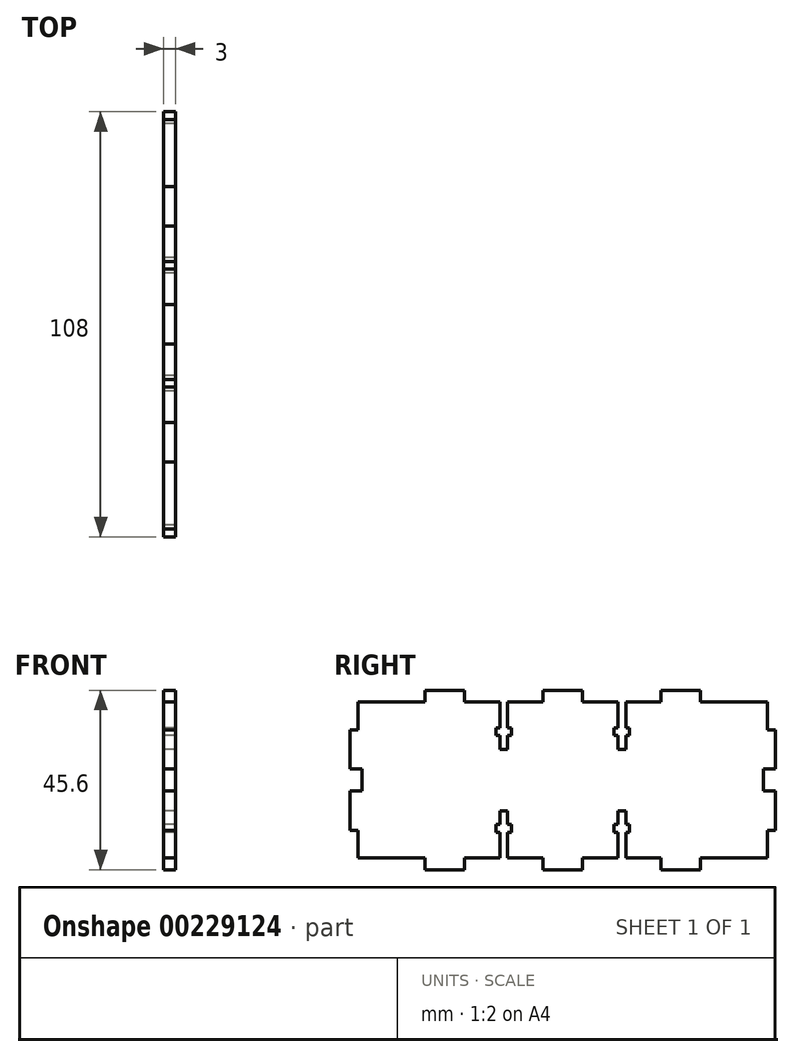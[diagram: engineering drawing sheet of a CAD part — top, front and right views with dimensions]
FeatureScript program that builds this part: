
annotation { "Feature Type Name" : "Feature", "Feature Type Description" : "" }
export const myFeature = defineFeature(function(context is Context, id is Id, definition is map)
    precondition{}
    {
        {
            var Q0;
            Q0=qCreatedBy(makeId("Right.planeOp"),FACE);
            var sketch = newSketch(context, id + "F0", { "sketchPlane" : qUnion([Q0])});
            skLineSegment(sketch, "E0", {"start": v(2.73, 33.75) * mm, "end": v(2.73, -11.85) * mm, "construction": true});
            skLineSegment(sketch, "E1.MirrorCS", {"start": v(16.73, 22.25) * mm, "end": v(15.73, 22.25) * mm});
            skLineSegment(sketch, "E2.MirrorCS", {"start": v(19.73, 22.25) * mm, "end": v(18.73, 22.25) * mm});
            skLineSegment(sketch, "E3.MirrorCS", {"start": v(18.73, 24.25) * mm, "end": v(19.73, 24.25) * mm});
            skLineSegment(sketch, "E4.MirrorCS", {"start": v(19.73, 24.25) * mm, "end": v(19.73, 22.25) * mm});
            skLineSegment(sketch, "E5.MirrorCS", {"start": v(19.73, -2.35) * mm, "end": v(19.73, -0.35) * mm});
            skLineSegment(sketch, "E6.MirrorCS", {"start": v(18.73, -2.35) * mm, "end": v(19.73, -2.35) * mm});
            skLineSegment(sketch, "E7.MirrorCS", {"start": v(15.73, 22.25) * mm, "end": v(15.73, 24.25) * mm});
            skLineSegment(sketch, "E8.MirrorCS", {"start": v(15.73, 24.25) * mm, "end": v(16.73, 24.25) * mm});
            skLineSegment(sketch, "E9.MirrorCS", {"start": v(19.73, -0.35) * mm, "end": v(18.73, -0.35) * mm});
            skLineSegment(sketch, "E10.MirrorCS", {"start": v(15.73, -0.35) * mm, "end": v(15.73, -2.35) * mm});
            skLineSegment(sketch, "E11.MirrorCS", {"start": v(16.73, -0.35) * mm, "end": v(15.73, -0.35) * mm});
            skLineSegment(sketch, "E12.MirrorCS", {"start": v(18.73, 22.25) * mm, "end": v(18.73, 18.75) * mm});
            skLineSegment(sketch, "E13.MirrorCS", {"start": v(53.73, 8.15) * mm, "end": v(53.73, 10.95) * mm});
            skLineSegment(sketch, "E14.MirrorCS", {"start": v(16.73, 18.75) * mm, "end": v(16.73, 22.25) * mm});
            skLineSegment(sketch, "E15.MirrorCS", {"start": v(53.73, 13.75) * mm, "end": v(53.73, 10.95) * mm});
            skLineSegment(sketch, "E16.MirrorCS", {"start": v(15.73, -2.35) * mm, "end": v(16.73, -2.35) * mm});
            skLineSegment(sketch, "E17.MirrorCS", {"start": v(27.73, -11.85) * mm, "end": v(27.73, -8.85) * mm});
            skLineSegment(sketch, "E18.MirrorCS", {"start": v(16.73, -2.35) * mm, "end": v(16.73, -8.85) * mm});
            skLineSegment(sketch, "E19.MirrorCS", {"start": v(7.73, -11.85) * mm, "end": v(2.73, -11.85) * mm});
            skLineSegment(sketch, "E20.MirrorCS", {"start": v(56.73, 8.15) * mm, "end": v(53.73, 8.15) * mm});
            skLineSegment(sketch, "E21.MirrorCS", {"start": v(7.73, 30.75) * mm, "end": v(7.73, 33.75) * mm});
            skLineSegment(sketch, "E22.MirrorCS", {"start": v(18.73, -0.35) * mm, "end": v(18.73, 3.15) * mm});
            skLineSegment(sketch, "E23.MirrorCS", {"start": v(18.73, -8.85) * mm, "end": v(18.73, -2.35) * mm});
            skLineSegment(sketch, "E24.MirrorCS", {"start": v(37.73, -8.85) * mm, "end": v(37.73, -11.85) * mm});
            skLineSegment(sketch, "E25.MirrorCS", {"start": v(54.73, 23.75) * mm, "end": v(56.73, 23.75) * mm});
            skLineSegment(sketch, "E26.MirrorCS", {"start": v(56.73, 13.75) * mm, "end": v(53.73, 13.75) * mm});
            skLineSegment(sketch, "E27.MirrorCS", {"start": v(16.73, 3.15) * mm, "end": v(16.73, -0.35) * mm});
            skLineSegment(sketch, "E28.MirrorCS", {"start": v(7.73, 33.75) * mm, "end": v(2.73, 33.75) * mm});
            skLineSegment(sketch, "E29.MirrorCS", {"start": v(37.73, 30.75) * mm, "end": v(37.73, 33.75) * mm});
            skLineSegment(sketch, "E30.MirrorCS", {"start": v(7.73, -8.85) * mm, "end": v(7.73, -11.85) * mm});
            skLineSegment(sketch, "E31.MirrorCS", {"start": v(27.73, 33.75) * mm, "end": v(27.73, 30.75) * mm});
            skLineSegment(sketch, "E32.MirrorCS", {"start": v(16.73, 3.15) * mm, "end": v(18.73, 3.15) * mm});
            skLineSegment(sketch, "E33.MirrorCS", {"start": v(16.73, 18.75) * mm, "end": v(18.73, 18.75) * mm});
            skLineSegment(sketch, "E34.MirrorCS", {"start": v(54.73, -1.85) * mm, "end": v(56.73, -1.85) * mm});
            skLineSegment(sketch, "E35.MirrorCS", {"start": v(16.73, 24.25) * mm, "end": v(16.73, 30.75) * mm});
            skPoint(sketch, "E36.MirrorP", {"position": v(18.23, 22.25) * mm});
            skLineSegment(sketch, "E37.MirrorCS", {"start": v(18.73, 30.75) * mm, "end": v(18.73, 24.25) * mm});
            skLineSegment(sketch, "E38.MirrorCS", {"start": v(37.73, -11.85) * mm, "end": v(27.73, -11.85) * mm});
            skLineSegment(sketch, "E39.MirrorCS", {"start": v(53.73, 10.95) * mm, "end": v(4.73, 10.95) * mm, "construction": true});
            skPoint(sketch, "E40.MirrorP", {"position": v(18.23, -0.35) * mm});
            skLineSegment(sketch, "E41.MirrorCS", {"start": v(16.73, -8.85) * mm, "end": v(7.73, -8.85) * mm});
            skPoint(sketch, "E42.MirrorP", {"position": v(18.23, 24.25) * mm});
            skLineSegment(sketch, "E43.MirrorCS", {"start": v(27.73, -8.85) * mm, "end": v(18.73, -8.85) * mm});
            skLineSegment(sketch, "E44.MirrorCS", {"start": v(54.73, -8.85) * mm, "end": v(37.73, -8.85) * mm});
            skPoint(sketch, "E45.MirrorP", {"position": v(18.23, -2.35) * mm});
            skLineSegment(sketch, "E46.MirrorCS", {"start": v(54.73, 30.75) * mm, "end": v(54.73, 23.75) * mm});
            skLineSegment(sketch, "E47.MirrorCS", {"start": v(56.73, 23.75) * mm, "end": v(56.73, 13.75) * mm});
            skLineSegment(sketch, "E48.MirrorCS", {"start": v(56.73, -1.85) * mm, "end": v(56.73, 8.15) * mm});
            skLineSegment(sketch, "E49.MirrorCS", {"start": v(54.73, 30.75) * mm, "end": v(37.73, 30.75) * mm});
            skLineSegment(sketch, "E50.MirrorCS", {"start": v(37.73, 33.75) * mm, "end": v(27.73, 33.75) * mm});
            skLineSegment(sketch, "E51.MirrorCS", {"start": v(27.73, 30.75) * mm, "end": v(18.73, 30.75) * mm});
            skLineSegment(sketch, "E52.MirrorCS", {"start": v(54.73, -8.85) * mm, "end": v(54.73, -1.85) * mm});
            skLineSegment(sketch, "E53.MirrorCS", {"start": v(16.73, 30.75) * mm, "end": v(7.73, 30.75) * mm});
            skLineSegment(sketch, "E54.MirrorCS", {"start": v(-14.27, -0.35) * mm, "end": v(-13.27, -0.35) * mm});
            skLineSegment(sketch, "E55.MirrorCS", {"start": v(-10.27, 22.25) * mm, "end": v(-10.27, 24.25) * mm});
            skLineSegment(sketch, "E56.MirrorCS", {"start": v(-11.27, 22.25) * mm, "end": v(-10.27, 22.25) * mm});
            skLineSegment(sketch, "E57.MirrorCS", {"start": v(-14.27, -2.35) * mm, "end": v(-14.27, -0.35) * mm});
            skLineSegment(sketch, "E58.MirrorCS", {"start": v(-14.27, 22.25) * mm, "end": v(-13.27, 22.25) * mm});
            skLineSegment(sketch, "E59.MirrorCS", {"start": v(-13.27, 24.25) * mm, "end": v(-14.27, 24.25) * mm});
            skLineSegment(sketch, "E60.MirrorCS", {"start": v(-10.27, -2.35) * mm, "end": v(-11.27, -2.35) * mm});
            skLineSegment(sketch, "E61.MirrorCS", {"start": v(-10.27, 24.25) * mm, "end": v(-11.27, 24.25) * mm});
            skLineSegment(sketch, "E62.MirrorCS", {"start": v(-14.27, 24.25) * mm, "end": v(-14.27, 22.25) * mm});
            skLineSegment(sketch, "E63.MirrorCS", {"start": v(-13.27, -2.35) * mm, "end": v(-14.27, -2.35) * mm});
            skLineSegment(sketch, "E64.MirrorCS", {"start": v(-22.27, 33.75) * mm, "end": v(-22.27, 30.75) * mm});
            skLineSegment(sketch, "E65.MirrorCS", {"start": v(-51.27, 13.75) * mm, "end": v(-48.27, 13.75) * mm});
            skLineSegment(sketch, "E66.MirrorCS", {"start": v(-48.27, 8.15) * mm, "end": v(-48.27, 10.95) * mm});
            skLineSegment(sketch, "E67.MirrorCS", {"start": v(-11.27, 18.75) * mm, "end": v(-11.27, 22.25) * mm});
            skLineSegment(sketch, "E68.MirrorCS", {"start": v(-32.27, 30.75) * mm, "end": v(-32.27, 33.75) * mm});
            skLineSegment(sketch, "E69.MirrorCS", {"start": v(-51.27, 8.15) * mm, "end": v(-48.27, 8.15) * mm});
            skLineSegment(sketch, "E70.MirrorCS", {"start": v(-2.27, 30.75) * mm, "end": v(-2.27, 33.75) * mm});
            skLineSegment(sketch, "E71.MirrorCS", {"start": v(-13.27, 22.25) * mm, "end": v(-13.27, 18.75) * mm});
            skLineSegment(sketch, "E72.MirrorCS", {"start": v(-11.27, -0.35) * mm, "end": v(-10.27, -0.35) * mm});
            skLineSegment(sketch, "E73.MirrorCS", {"start": v(-13.27, -0.35) * mm, "end": v(-13.27, 3.15) * mm});
            skLineSegment(sketch, "E74.MirrorCS", {"start": v(-2.27, -8.85) * mm, "end": v(-2.27, -11.85) * mm});
            skLineSegment(sketch, "E75.MirrorCS", {"start": v(-11.27, 3.15) * mm, "end": v(-11.27, -0.35) * mm});
            skLineSegment(sketch, "E76.MirrorCS", {"start": v(-22.27, -11.85) * mm, "end": v(-22.27, -8.85) * mm});
            skLineSegment(sketch, "E77.MirrorCS", {"start": v(-11.27, 3.15) * mm, "end": v(-13.27, 3.15) * mm});
            skLineSegment(sketch, "E78.MirrorCS", {"start": v(-11.27, 18.75) * mm, "end": v(-13.27, 18.75) * mm});
            skLineSegment(sketch, "E79.MirrorCS", {"start": v(-49.27, 23.75) * mm, "end": v(-51.27, 23.75) * mm});
            skLineSegment(sketch, "E80.MirrorCS", {"start": v(-32.27, -8.85) * mm, "end": v(-32.27, -11.85) * mm});
            skLineSegment(sketch, "E81.MirrorCS", {"start": v(-10.27, -0.35) * mm, "end": v(-10.27, -2.35) * mm});
            skLineSegment(sketch, "E82.MirrorCS", {"start": v(-49.27, -1.85) * mm, "end": v(-51.27, -1.85) * mm});
            skLineSegment(sketch, "E83.MirrorCS", {"start": v(-48.27, 13.75) * mm, "end": v(-48.27, 10.95) * mm});
            skLineSegment(sketch, "E84.MirrorCS", {"start": v(-22.27, 30.75) * mm, "end": v(-13.27, 30.75) * mm});
            skLineSegment(sketch, "E85.MirrorCS", {"start": v(-13.27, 30.75) * mm, "end": v(-13.27, 24.25) * mm});
            skLineSegment(sketch, "E86.MirrorCS", {"start": v(-48.27, 10.95) * mm, "end": v(0.73, 10.95) * mm, "construction": true});
            skPoint(sketch, "E87.MirrorP", {"position": v(-12.77, -0.35) * mm});
            skLineSegment(sketch, "E88.MirrorCS", {"start": v(-11.27, 24.25) * mm, "end": v(-11.27, 30.75) * mm});
            skLineSegment(sketch, "E89.MirrorCS", {"start": v(-32.27, 33.75) * mm, "end": v(-22.27, 33.75) * mm});
            skPoint(sketch, "E90.MirrorP", {"position": v(-12.77, -2.35) * mm});
            skLineSegment(sketch, "E91.MirrorCS", {"start": v(-49.27, 30.75) * mm, "end": v(-32.27, 30.75) * mm});
            skLineSegment(sketch, "E92.MirrorCS", {"start": v(-49.27, -8.85) * mm, "end": v(-49.27, -1.85) * mm});
            skPoint(sketch, "E93.MirrorP", {"position": v(-12.77, 24.25) * mm});
            skLineSegment(sketch, "E94.MirrorCS", {"start": v(-22.27, -8.85) * mm, "end": v(-13.27, -8.85) * mm});
            skLineSegment(sketch, "E95.MirrorCS", {"start": v(-13.27, -8.85) * mm, "end": v(-13.27, -2.35) * mm});
            skLineSegment(sketch, "E96.MirrorCS", {"start": v(-32.27, -11.85) * mm, "end": v(-22.27, -11.85) * mm});
            skLineSegment(sketch, "E97.MirrorCS", {"start": v(-49.27, -8.85) * mm, "end": v(-32.27, -8.85) * mm});
            skLineSegment(sketch, "E98.MirrorCS", {"start": v(-49.27, 30.75) * mm, "end": v(-49.27, 23.75) * mm});
            skPoint(sketch, "E99.MirrorP", {"position": v(-12.77, 22.25) * mm});
            skLineSegment(sketch, "E100.MirrorCS", {"start": v(-11.27, -2.35) * mm, "end": v(-11.27, -8.85) * mm});
            skLineSegment(sketch, "E101.MirrorCS", {"start": v(-11.27, -8.85) * mm, "end": v(-2.27, -8.85) * mm});
            skLineSegment(sketch, "E102.MirrorCS", {"start": v(-11.27, 30.75) * mm, "end": v(-2.27, 30.75) * mm});
            skLineSegment(sketch, "E103.MirrorCS", {"start": v(-51.27, 23.75) * mm, "end": v(-51.27, 13.75) * mm});
            skLineSegment(sketch, "E104.MirrorCS", {"start": v(-51.27, -1.85) * mm, "end": v(-51.27, 8.15) * mm});
            skLineSegment(sketch, "E105", {"start": v(-2.27, 33.75) * mm, "end": v(2.73, 33.75) * mm});
            skLineSegment(sketch, "E106", {"start": v(-2.27, -11.85) * mm, "end": v(2.73, -11.85) * mm});
            skSolve(sketch);
        }
        {
            var Q0;
            Q0 = qSketchRegion(id + "F0", true);
            extrude(context, id + "F1", {"entities" : qUnion([Q0]), "depth" : 3 * mm});
        }
    });
